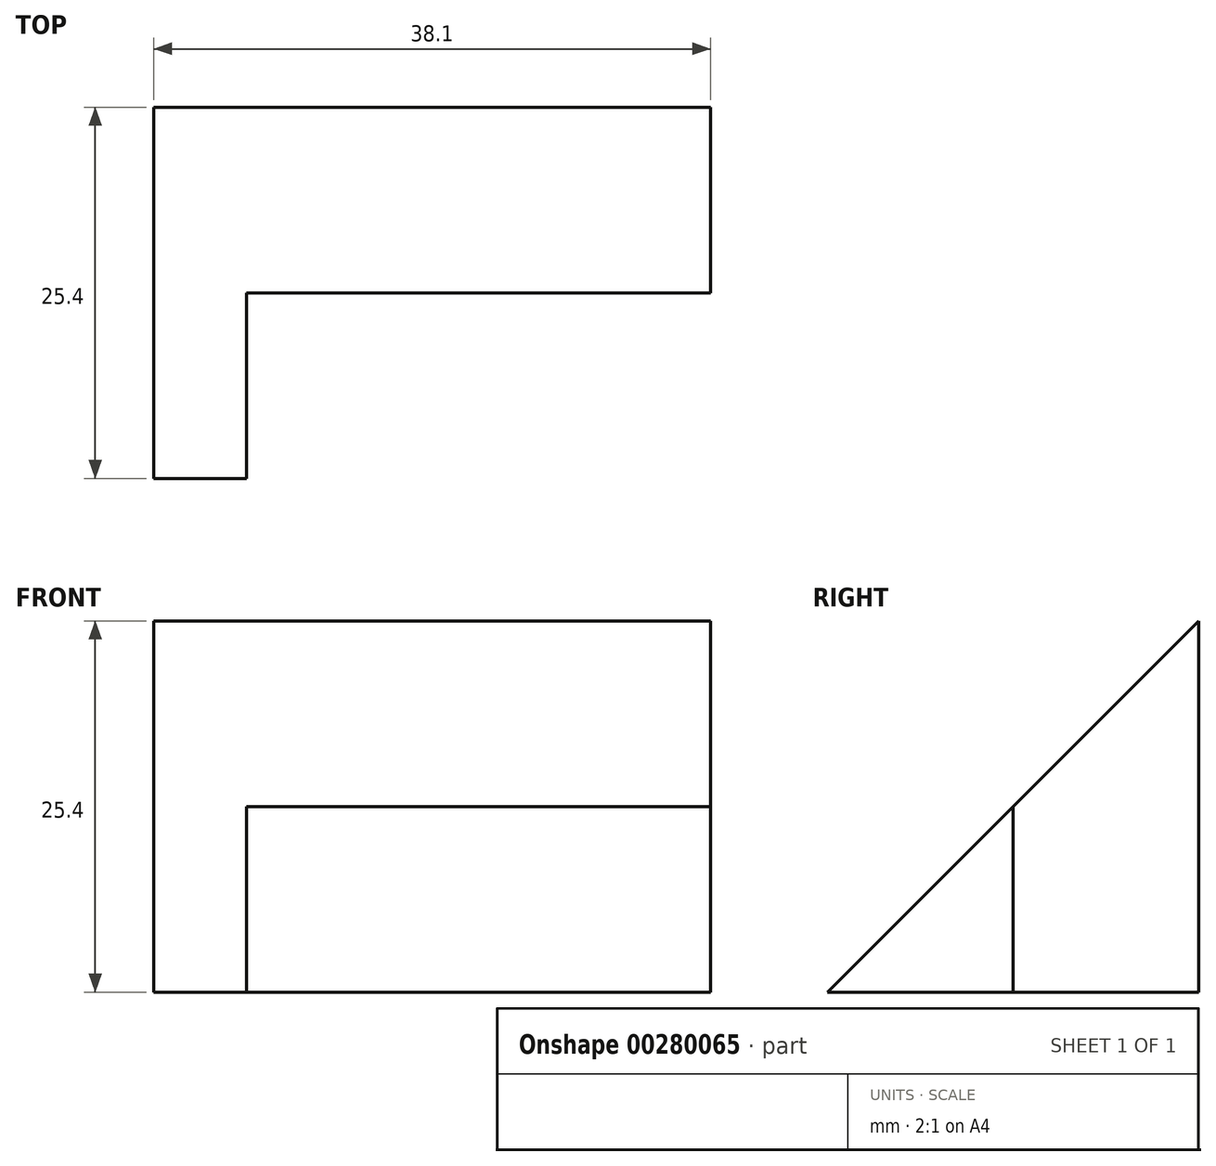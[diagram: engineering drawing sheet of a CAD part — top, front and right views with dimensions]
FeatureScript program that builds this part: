
annotation { "Feature Type Name" : "Feature", "Feature Type Description" : "" }
export const myFeature = defineFeature(function(context is Context, id is Id, definition is map)
    precondition{}
    {
        {
            var Q0;
            Q0=qCreatedBy(makeId("Right.planeOp"),FACE);
            var sketch = newSketch(context, id + "F0", { "sketchPlane" : qUnion([Q0])});
            skLineSegment(sketch, "E0", {"start": v(25.4, 0) * mm, "end": v(25.4, 25.4) * mm});
            skLineSegment(sketch, "E1", {"start": v(25.4, 25.4) * mm, "end": v(12.7, 12.7) * mm});
            skLineSegment(sketch, "E2", {"start": v(25.4, 0) * mm, "end": v(12.7, 0) * mm});
            skLineSegment(sketch, "E3", {"start": v(12.7, 12.7) * mm, "end": v(12.7, 0) * mm});
            skSolve(sketch);
        }
        {
            var Q0;
            Q0=makeQuery(id+"F0.imprint","IMPRINT",FACE,{"disambiguationData":[TD([[makeQuery(id+"F0.imprint","IMPRINT",EDGE,{"derivedFrom":sQuery(id+"F0.wireOp",EDGE,"E0")}),1.0]])]});
            extrude(context, id + "F1", {"entities" : qUnion([Q0]), "depth" : 38.1 * mm});
        }
        {
            var Q0;
            Q0=qCreatedBy(makeId("Right.planeOp"),FACE);
            var sketch = newSketch(context, id + "F2", { "sketchPlane" : qUnion([Q0])});
            skLineSegment(sketch, "E4", {"start": v(0, 0) * mm, "end": v(12.7, 0) * mm});
            skLineSegment(sketch, "E5", {"start": v(12.7, 0) * mm, "end": v(12.7, 12.7) * mm});
            skLineSegment(sketch, "E6", {"start": v(12.7, 12.7) * mm, "end": v(0, 0) * mm});
            skSolve(sketch);
        }
        {
            var Q0;
            Q0 = qSketchRegion(id + "F2", true);
            extrude(context, id + "F3", {"entities" : qUnion([Q0]), "operationType" : NewBodyOperationType.ADD, "depth" : 6.35 * mm});
        }
        {
            var Q0;
            Q0=makeQuery(id+"F1.opExtrude","CAP_FACE",FACE,{"disambiguationData":[OSD([sQuery(id+"F0.wireOp",EDGE,"E0"),sQuery(id+"F0.wireOp",EDGE,"E1"),sQuery(id+"F0.wireOp",EDGE,"E2"),sQuery(id+"F0.wireOp",EDGE,"E3")])],"isStart":false});
            var sketch = newSketch(context, id + "F4", { "sketchPlane" : qUnion([Q0])});
            skSolve(sketch);
        }
        {
            var Q0;
            Q0=makeQuery(id+"F3.boolean.opBoolean","MERGE",FACE,{"derivedFrom":[makeQuery(id+"F1.opExtrude","CAP_FACE",FACE,{"disambiguationData":[OSD([sQuery(id+"F0.wireOp",EDGE,"E0"),sQuery(id+"F0.wireOp",EDGE,"E1"),sQuery(id+"F0.wireOp",EDGE,"E2"),sQuery(id+"F0.wireOp",EDGE,"E3")])],"isStart":true}),makeQuery(id+"F3.opExtrude","CAP_FACE",FACE,{"disambiguationData":[OSD([sQuery(id+"F2.wireOp",EDGE,"E4"),sQuery(id+"F2.wireOp",EDGE,"E5"),sQuery(id+"F2.wireOp",EDGE,"E6")])],"isStart":true})]});
            var sketch = newSketch(context, id + "F5", { "sketchPlane" : qUnion([Q0])});
            skLineSegment(sketch, "E7", {"start": v(0, 0) * mm, "end": v(-12.7, 0) * mm});
            skLineSegment(sketch, "E8", {"start": v(-12.7, 0) * mm, "end": v(-12.7, 12.7) * mm});
            skPoint(sketch, "E8.endSnap0", {"position": v(-12.7, 12.7) * mm});
            skSolve(sketch);
        }
        {
            var Q0;
            Q0=makeQuery(id+"F4.imprint","IMPRINT",FACE,{"disambiguationData":[TD([[makeQuery(id+"F4.imprint","IMPRINT",EDGE,{"derivedFrom":makeQuery(id+"F1.opExtrude","CAP_EDGE",EDGE,{"disambiguationData":[OSD([sQuery(id+"F0.wireOp",EDGE,"E0")])],"isStart":false})}),1.0]])]});
            var sketch = newSketch(context, id + "F6", { "sketchPlane" : qUnion([Q0])});
            skLineSegment(sketch, "E9", {"start": v(12.69, 12.66) * mm, "end": v(0, 0) * mm});
            skLineSegment(sketch, "E10", {"start": v(0, 0) * mm, "end": v(12.69, 0) * mm});
            skLineSegment(sketch, "E11", {"start": v(12.69, 0) * mm, "end": v(12.69, 12.66) * mm});
            skSolve(sketch);
        }
        {
            var Q0;
            Q0=sQuery(id+"F6.wireOp",EDGE,"E9");
            extrude(context, id + "F7", {"bodyType" : ToolBodyType.SURFACE, "surfaceEntities" : qUnion([Q0]), "oppositeDirection" : true, "depth" : 6.35 * mm});
        }
    });
